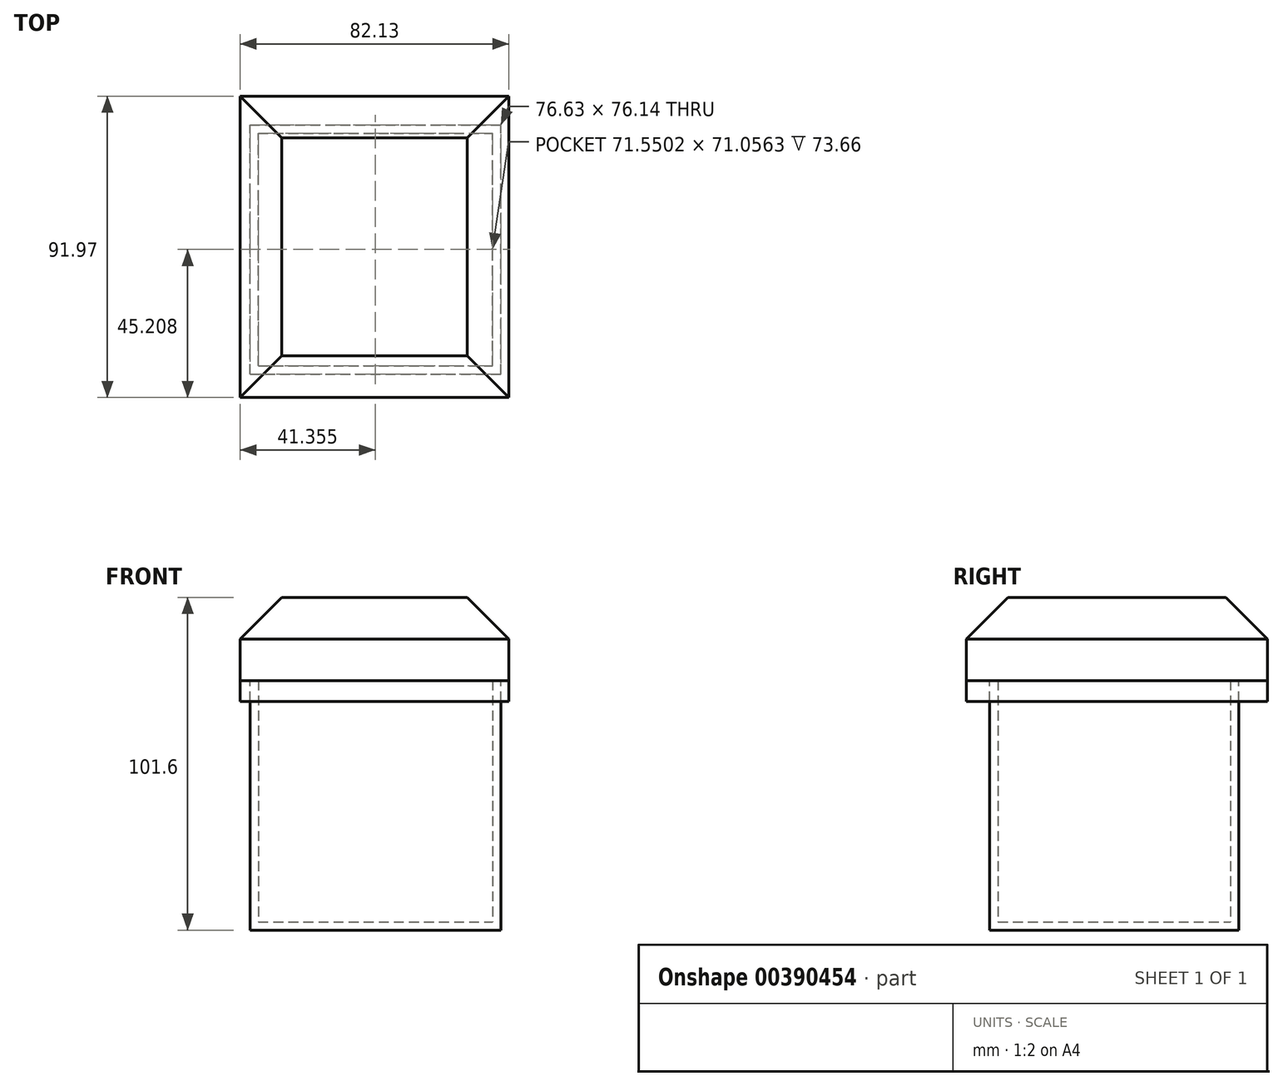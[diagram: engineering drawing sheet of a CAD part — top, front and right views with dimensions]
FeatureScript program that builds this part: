
annotation { "Feature Type Name" : "Feature", "Feature Type Description" : "" }
export const myFeature = defineFeature(function(context is Context, id is Id, definition is map)
    precondition{}
    {
        {
            var Q0;
            Q0=qCreatedBy(makeId("Top.planeOp"),FACE);
            var sketch = newSketch(context, id + "F0", { "sketchPlane" : qUnion([Q0])});
            skLineSegment(sketch, "E0.bottom", {"start": v(0, 0) * mm, "end": v(76.63, 0) * mm});
            skLineSegment(sketch, "E0.top", {"start": v(0, 76.14) * mm, "end": v(76.63, 76.14) * mm});
            skLineSegment(sketch, "E0.left", {"start": v(0, 0) * mm, "end": v(0, 76.14) * mm});
            skLineSegment(sketch, "E0.right", {"start": v(76.63, 0) * mm, "end": v(76.63, 76.14) * mm});
            skSolve(sketch);
        }
        {
            var Q0;
            Q0 = qSketchRegion(id + "F0", true);
            extrude(context, id + "F1", {"entities" : qUnion([Q0]), "depth" : 76.2 * mm});
        }
        {
            var Q0;
            Q0=makeQuery(id+"F1.opExtrude","CAP_FACE",FACE,{"disambiguationData":[OSD([sQuery(id+"F0.wireOp",EDGE,"E0.bottom"),sQuery(id+"F0.wireOp",EDGE,"E0.top"),sQuery(id+"F0.wireOp",EDGE,"E0.left"),sQuery(id+"F0.wireOp",EDGE,"E0.right")])],"isStart":false});
            shell(context, id + "F2", {"entities" : qUnion([Q0]), "thickness" : 2.54 * mm});
        }
        {
            var Q0;
            Q0=makeQuery(id+"F1.opExtrude","CAP_FACE",FACE,{"disambiguationData":[OSD([sQuery(id+"F0.wireOp",EDGE,"E0.bottom"),sQuery(id+"F0.wireOp",EDGE,"E0.top"),sQuery(id+"F0.wireOp",EDGE,"E0.left"),sQuery(id+"F0.wireOp",EDGE,"E0.right")])],"isStart":false});
            var sketch = newSketch(context, id + "F3", { "sketchPlane" : qUnion([Q0])});
            skLineSegment(sketch, "E1.bottom", {"start": v(-3.04, -7.14) * mm, "end": v(79.09, -7.14) * mm});
            skLineSegment(sketch, "E1.top", {"start": v(-3.04, 84.83) * mm, "end": v(79.09, 84.83) * mm});
            skLineSegment(sketch, "E1.left", {"start": v(-3.04, -7.14) * mm, "end": v(-3.04, 84.83) * mm});
            skLineSegment(sketch, "E1.right", {"start": v(79.09, -7.14) * mm, "end": v(79.09, 84.83) * mm});
            skLineSegment(sketch, "E2.bottom", {"start": v(0, 76.14) * mm, "end": v(76.63, 76.14) * mm});
            skLineSegment(sketch, "E2.top", {"start": v(0, 0) * mm, "end": v(76.63, 0) * mm});
            skLineSegment(sketch, "E2.left", {"start": v(0, 76.14) * mm, "end": v(0, 0) * mm});
            skLineSegment(sketch, "E2.right", {"start": v(76.63, 76.14) * mm, "end": v(76.63, 0) * mm});
            skSolve(sketch);
        }
        {
            var Q0;
            Q0 = qSketchRegion(id + "F3", true);
            extrude(context, id + "F4", {"entities" : qUnion([Q0]), "oppositeDirection" : true, "depth" : 6.35 * mm});
        }
        {
            var Q0;
            Q0=makeQuery(id+"F4.opExtrude","CAP_FACE",FACE,{"disambiguationData":[OSD([sQuery(id+"F3.wireOp",EDGE,"E1.bottom"),sQuery(id+"F3.wireOp",EDGE,"E1.top"),sQuery(id+"F3.wireOp",EDGE,"E1.left"),sQuery(id+"F3.wireOp",EDGE,"E1.right"),sQuery(id+"F3.wireOp",EDGE,"E2.bottom"),sQuery(id+"F3.wireOp",EDGE,"E2.top"),sQuery(id+"F3.wireOp",EDGE,"E2.left"),sQuery(id+"F3.wireOp",EDGE,"E2.right")])],"isStart":true});
            var sketch = newSketch(context, id + "F5", { "sketchPlane" : qUnion([Q0])});
            skLineSegment(sketch, "E3.bottom", {"start": v(79.09, -7.14) * mm, "end": v(-3.04, -7.14) * mm});
            skLineSegment(sketch, "E3.top", {"start": v(79.09, 84.83) * mm, "end": v(-3.04, 84.83) * mm});
            skLineSegment(sketch, "E3.left", {"start": v(79.09, -7.14) * mm, "end": v(79.09, 84.83) * mm});
            skLineSegment(sketch, "E3.right", {"start": v(-3.04, -7.14) * mm, "end": v(-3.04, 84.83) * mm});
            skSolve(sketch);
        }
        {
            var Q0;
            Q0 = qSketchRegion(id + "F5", true);
            extrude(context, id + "F6", {"entities" : qUnion([Q0]), "depth" : 25.4 * mm});
        }
        {
            var Q0;
            Q0=makeQuery(id+"F6.opExtrude","CAP_EDGE",EDGE,{"disambiguationData":[OSD([sQuery(id+"F5.wireOp",EDGE,"E3.bottom")])],"isStart":false});
            var Q1;
            Q1=makeQuery(id+"F6.opExtrude","CAP_EDGE",EDGE,{"disambiguationData":[OSD([sQuery(id+"F5.wireOp",EDGE,"E3.right")])],"isStart":false});
            var Q2;
            Q2=makeQuery(id+"F6.opExtrude","CAP_EDGE",EDGE,{"disambiguationData":[OSD([sQuery(id+"F5.wireOp",EDGE,"E3.top")])],"isStart":false});
            var Q3;
            Q3=makeQuery(id+"F6.opExtrude","CAP_EDGE",EDGE,{"disambiguationData":[OSD([sQuery(id+"F5.wireOp",EDGE,"E3.left")])],"isStart":false});
            chamfer(context, id + "F7", {"entities" : qUnion([Q0, Q1, Q2, Q3]), "width" : 12.7 * mm, "tangentPropagation" : true});
        }
    });
